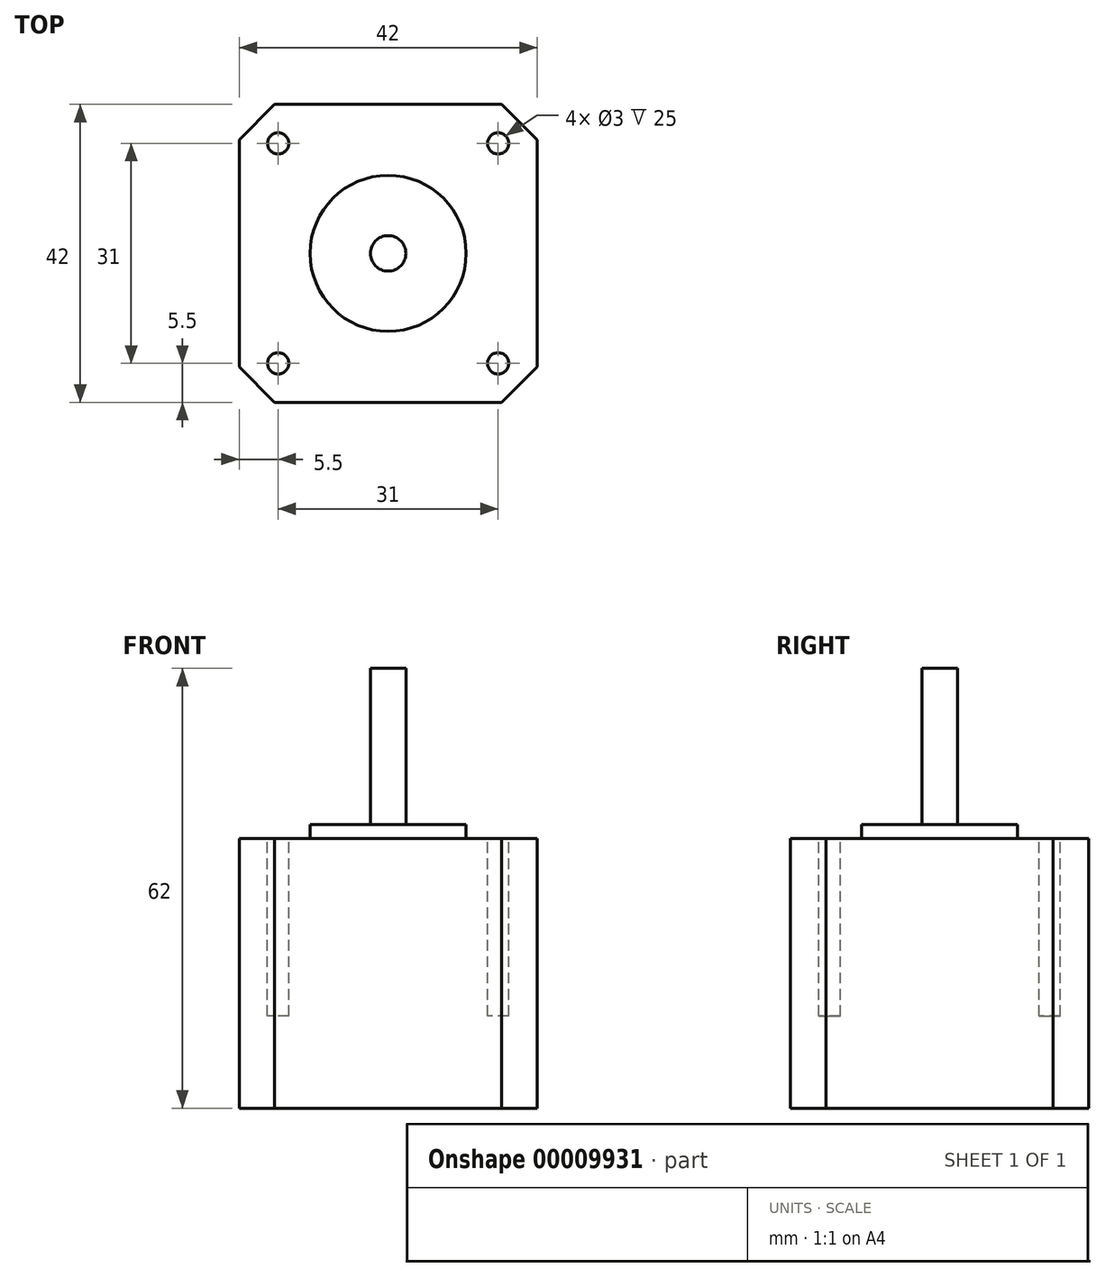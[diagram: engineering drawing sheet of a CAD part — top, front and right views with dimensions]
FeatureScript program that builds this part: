
annotation { "Feature Type Name" : "Feature", "Feature Type Description" : "" }
export const myFeature = defineFeature(function(context is Context, id is Id, definition is map)
    precondition{}
    {
        {
            var Q0;
            Q0=qCreatedBy(makeId("Top.planeOp"),FACE);
            var sketch = newSketch(context, id + "F0", { "sketchPlane" : qUnion([Q0])});
            skLineSegment(sketch, "E0.bottom", {"start": v(0, 0) * mm, "end": v(42, 0) * mm});
            skLineSegment(sketch, "E0.top", {"start": v(0, 42) * mm, "end": v(42, 42) * mm});
            skLineSegment(sketch, "E0.left", {"start": v(0, 0) * mm, "end": v(0, 42) * mm});
            skLineSegment(sketch, "E0.right", {"start": v(42, 0) * mm, "end": v(42, 42) * mm});
            skSolve(sketch);
        }
        {
            var Q0;
            Q0=qSketchRegion(id+"F0",true);
            extrude(context, id + "F1", {"entities" : qUnion([Q0]), "depth" : 38 * mm});
        }
        {
            var Q0;
            Q0=makeQuery(id+"F1.opExtrude","SWEPT_EDGE",EDGE,{"disambiguationData":[OSD([sQuery(id+"F0.wireOp",EDGE,"E0.bottom"),sQuery(id+"F0.wireOp",EDGE,"E0.left")])]});
            var Q1;
            Q1=makeQuery(id+"F1.opExtrude","SWEPT_EDGE",EDGE,{"disambiguationData":[OSD([sQuery(id+"F0.wireOp",EDGE,"E0.top"),sQuery(id+"F0.wireOp",EDGE,"E0.left")])]});
            var Q2;
            Q2=makeQuery(id+"F1.opExtrude","SWEPT_EDGE",EDGE,{"disambiguationData":[OSD([sQuery(id+"F0.wireOp",EDGE,"E0.bottom"),sQuery(id+"F0.wireOp",EDGE,"E0.right")])]});
            var Q3;
            Q3=makeQuery(id+"F1.opExtrude","SWEPT_EDGE",EDGE,{"disambiguationData":[OSD([sQuery(id+"F0.wireOp",EDGE,"E0.top"),sQuery(id+"F0.wireOp",EDGE,"E0.right")])]});
            chamfer(context, id + "F2", {"entities" : qUnion([Q0, Q1, Q2, Q3]), "width" : 5 * mm, "tangentPropagation" : true});
        }
        {
            var Q0;
            Q0=makeQuery(id+"F1.opExtrude","CAP_FACE",FACE,{"disambiguationData":[OSD([sQuery(id+"F0.wireOp",EDGE,"E0.bottom"),sQuery(id+"F0.wireOp",EDGE,"E0.top"),sQuery(id+"F0.wireOp",EDGE,"E0.left"),sQuery(id+"F0.wireOp",EDGE,"E0.right")])],"isStart":false});
            var sketch = newSketch(context, id + "F3", { "sketchPlane" : qUnion([Q0])});
            skCircle(sketch, "E1", {"center": v(21, 21) * mm, "radius": 11 * mm});
            skSolve(sketch);
        }
        {
            var Q0;
            Q0=qSketchRegion(id+"F3",true);
            extrude(context, id + "F4", {"entities" : qUnion([Q0]), "operationType" : NewBodyOperationType.ADD, "depth" : 2 * mm});
        }
        {
            var Q0;
            Q0=makeQuery(id+"F4.opExtrude","CAP_FACE",FACE,{"disambiguationData":[OSD([sQuery(id+"F3.wireOp",EDGE,"E1")])],"isStart":false});
            var sketch = newSketch(context, id + "F5", { "sketchPlane" : qUnion([Q0])});
            skCircle(sketch, "E2", {"center": v(21, 21) * mm, "radius": 2.5 * mm});
            skSolve(sketch);
        }
        {
            var Q0;
            Q0=qSketchRegion(id+"F5",true);
            extrude(context, id + "F6", {"entities" : qUnion([Q0]), "operationType" : NewBodyOperationType.ADD, "depth" : 22 * mm});
        }
        {
            var Q0;
            Q0=makeQuery(id+"F1.opExtrude","CAP_FACE",FACE,{"disambiguationData":[OSD([sQuery(id+"F0.wireOp",EDGE,"E0.bottom"),sQuery(id+"F0.wireOp",EDGE,"E0.top"),sQuery(id+"F0.wireOp",EDGE,"E0.left"),sQuery(id+"F0.wireOp",EDGE,"E0.right")])],"isStart":false});
            var sketch = newSketch(context, id + "F7", { "sketchPlane" : qUnion([Q0])});
            skCircle(sketch, "E3", {"center": v(5.5, 36.5) * mm, "radius": 1.5 * mm});
            skCircle(sketch, "E4", {"center": v(5.5, 5.5) * mm, "radius": 1.5 * mm});
            skCircle(sketch, "E5", {"center": v(36.5, 36.5) * mm, "radius": 1.5 * mm});
            skCircle(sketch, "E6", {"center": v(36.5, 5.5) * mm, "radius": 1.5 * mm});
            skSolve(sketch);
        }
        {
            var Q0;
            Q0=qSketchRegion(id+"F7",true);
            extrude(context, id + "F8", {"entities" : qUnion([Q0]), "operationType" : NewBodyOperationType.REMOVE, "oppositeDirection" : true, "depth" : 25 * mm});
        }
    });
